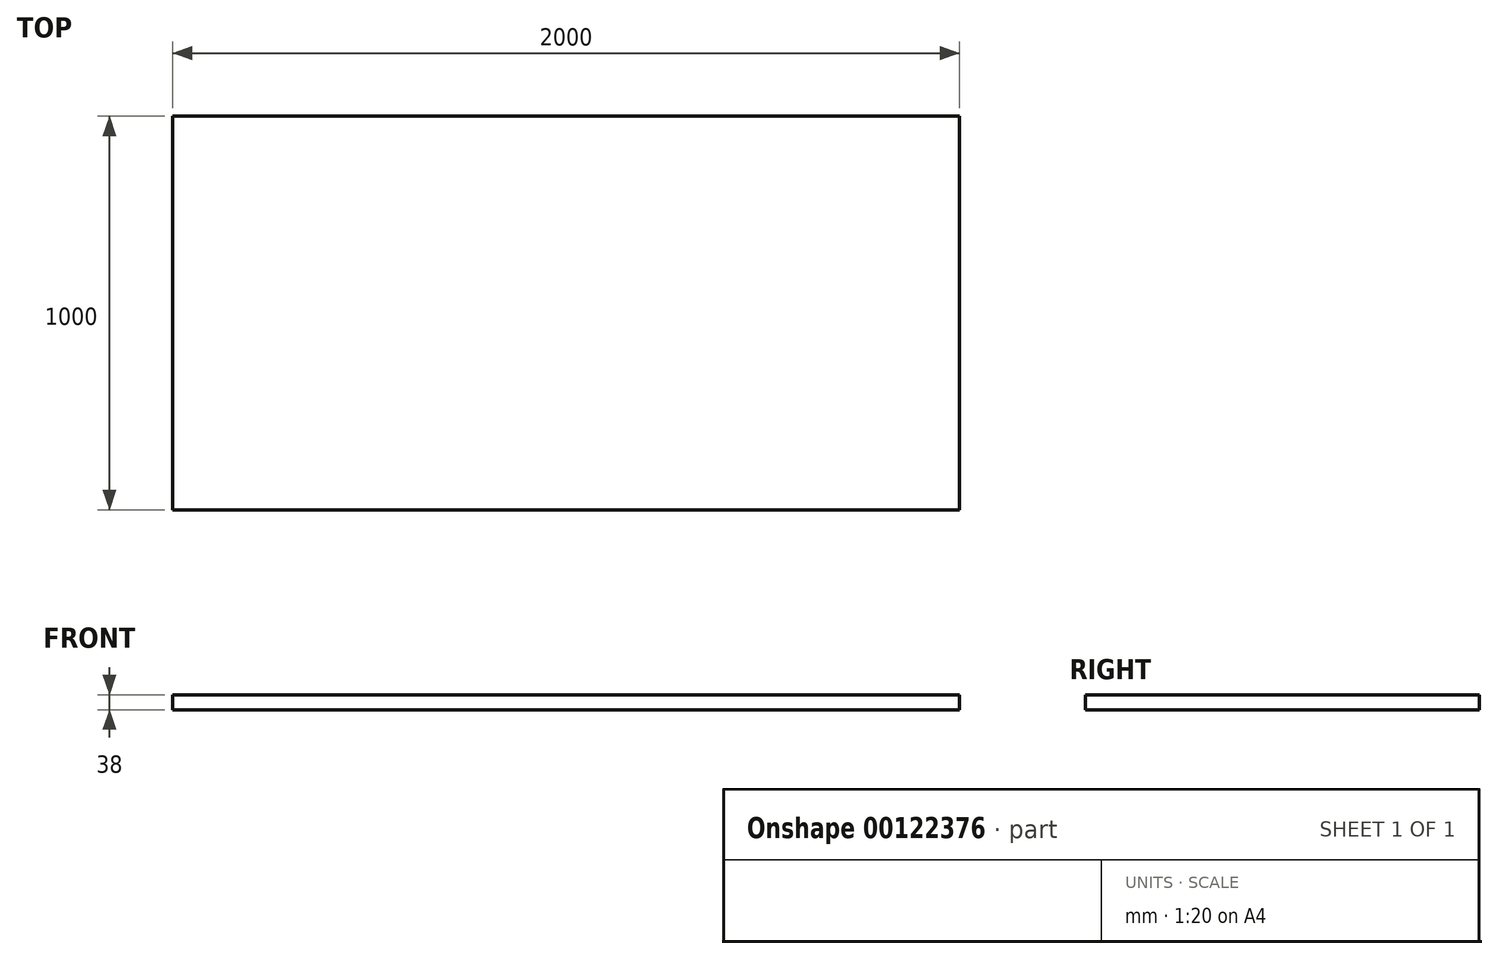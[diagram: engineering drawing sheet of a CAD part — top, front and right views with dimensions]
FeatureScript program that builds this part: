
annotation { "Feature Type Name" : "Feature", "Feature Type Description" : "" }
export const myFeature = defineFeature(function(context is Context, id is Id, definition is map)
    precondition{}
    {
        {
            var Q0;
            Q0=qCreatedBy(makeId("Top.planeOp"),FACE);
            var sketch = newSketch(context, id + "F0", { "sketchPlane" : qUnion([Q0])});
            skLineSegment(sketch, "E0.bottom", {"start": v(-1000, 500) * mm, "end": v(1000, 500) * mm});
            skLineSegment(sketch, "E0.top", {"start": v(-1000, -500) * mm, "end": v(1000, -500) * mm});
            skLineSegment(sketch, "E0.left", {"start": v(-1000, 500) * mm, "end": v(-1000, -500) * mm});
            skLineSegment(sketch, "E0.right", {"start": v(1000, 500) * mm, "end": v(1000, -500) * mm});
            skSolve(sketch);
        }
        {
            var Q0;
            Q0 = qSketchRegion(id + "F0", true);
            extrude(context, id + "F1", {"entities" : qUnion([Q0]), "depth" : 38 * mm});
        }
    });
